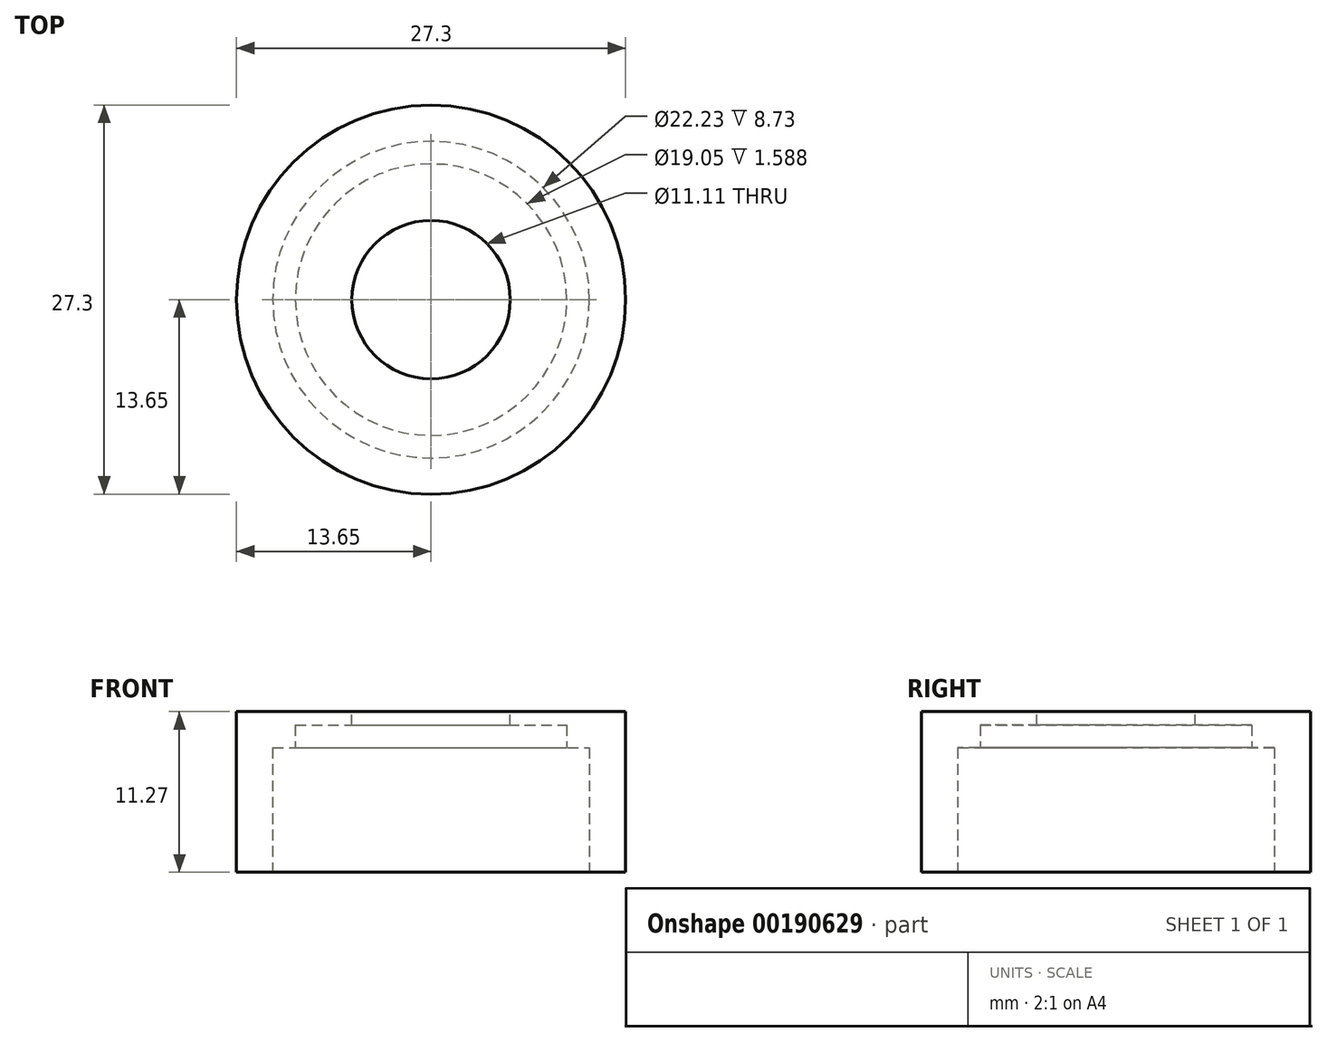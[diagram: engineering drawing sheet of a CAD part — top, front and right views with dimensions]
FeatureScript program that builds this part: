
annotation { "Feature Type Name" : "Feature", "Feature Type Description" : "" }
export const myFeature = defineFeature(function(context is Context, id is Id, definition is map)
    precondition{}
    {
        {
            var Q0;
            Q0=qCreatedBy(makeId("Top.planeOp"),FACE);
            var sketch = newSketch(context, id + "F0", { "sketchPlane" : qUnion([Q0])});
            skCircle(sketch, "E0", {"center": v(0, 0) * mm, "radius": 13.65 * mm});
            skSolve(sketch);
        }
        {
            var Q0;
            Q0 = qSketchRegion(id + "F0", true);
            extrude(context, id + "F1", {"entities" : qUnion([Q0]), "depth" : 11.27 * mm});
        }
        {
            var Q0;
            Q0=makeQuery(id+"F1.opExtrude","CAP_FACE",FACE,{"disambiguationData":[OSD([sQuery(id+"F0.wireOp",EDGE,"E0")])],"isStart":true});
            var sketch = newSketch(context, id + "F2", { "sketchPlane" : qUnion([Q0])});
            skCircle(sketch, "E1", {"center": v(0, 0) * mm, "radius": 11.11 * mm});
            skSolve(sketch);
        }
        {
            var Q0;
            Q0=makeQuery(id+"F2.imprint","IMPRINT",FACE,{"disambiguationData":[TD([[makeQuery(id+"F2.imprint","IMPRINT",EDGE,{"derivedFrom":sQuery(id+"F2.wireOp",EDGE,"E1")}),1.0]])]});
            extrude(context, id + "F3", {"entities" : qUnion([Q0]), "operationType" : NewBodyOperationType.REMOVE, "oppositeDirection" : true, "depth" : 8.73 * mm});
        }
        {
            var Q0;
            Q0=makeQuery(id+"F3.boolean.opBoolean","COPY",FACE,{"derivedFrom":makeQuery(id+"F3.opExtrude","CAP_FACE",FACE,{"disambiguationData":[OSD([sQuery(id+"F2.wireOp",EDGE,"E1")])],"isStart":false})});
            var sketch = newSketch(context, id + "F4", { "sketchPlane" : qUnion([Q0])});
            skCircle(sketch, "E2", {"center": v(0, 0) * mm, "radius": 9.53 * mm});
            skSolve(sketch);
        }
        {
            var Q0;
            Q0 = qSketchRegion(id + "F4", true);
            extrude(context, id + "F5", {"entities" : qUnion([Q0]), "operationType" : NewBodyOperationType.REMOVE, "oppositeDirection" : true, "depth" : 1.59 * mm});
        }
        {
            var Q0;
            Q0=makeQuery(id+"F1.opExtrude","CAP_FACE",FACE,{"disambiguationData":[OSD([sQuery(id+"F0.wireOp",EDGE,"E0")])],"isStart":false});
            var sketch = newSketch(context, id + "F6", { "sketchPlane" : qUnion([Q0])});
            skCircle(sketch, "E3", {"center": v(0, 0) * mm, "radius": 5.56 * mm});
            skSolve(sketch);
        }
        {
            var Q0;
            Q0=makeQuery(id+"F6.imprint","IMPRINT",FACE,{"disambiguationData":[TD([[makeQuery(id+"F6.imprint","IMPRINT",EDGE,{"derivedFrom":sQuery(id+"F6.wireOp",EDGE,"E3")}),1.0]])]});
            extrude(context, id + "F7", {"entities" : qUnion([Q0]), "operationType" : NewBodyOperationType.REMOVE, "endBound" : BoundingType.THROUGH_ALL, "oppositeDirection" : true, "depth" : 25.4 * mm});
        }
    });
